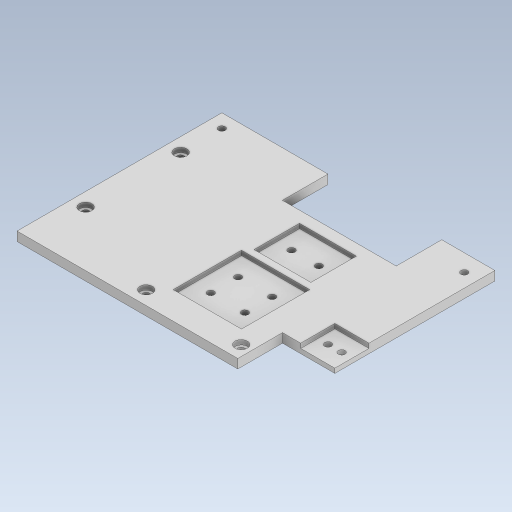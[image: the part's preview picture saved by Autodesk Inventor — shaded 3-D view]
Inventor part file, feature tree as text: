
AUTODESK INVENTOR PART (.ipt)
format: ipt  version: 2023.5 (Build 275446000, 446)  size: 178,688 bytes
history: native  units: in
note: dims shown in document units (in); Inventor stores cm internally (conversion verified against a paired STEP export)
features: extrude x2, sketch x1
ambient origin geometry x8: Origin, YZ Plane, XZ Plane, XY Plane, X Axis, Y Axis, Z Axis, Center Point
bodies: Solid1 (feature_tree)
feature tree (3):
  sketch  "Sketch1"  dims[d0=0.1575in d1=0.0in d2=0.0787in d3=0.0in d4=0.4724in d5=0.2953in d6=0.4724in d7=0.3543in d8=0.0in d10=0.0in d12=0.315in d13=0.2165in d14=0.2165in d15=0.2165in d16=0.2165in]
  extrude  "Extrusion1"  Depth=0.0787in TaperAngle=0.0deg
  extrude  "Extrusion2"  Depth=0.4724in
